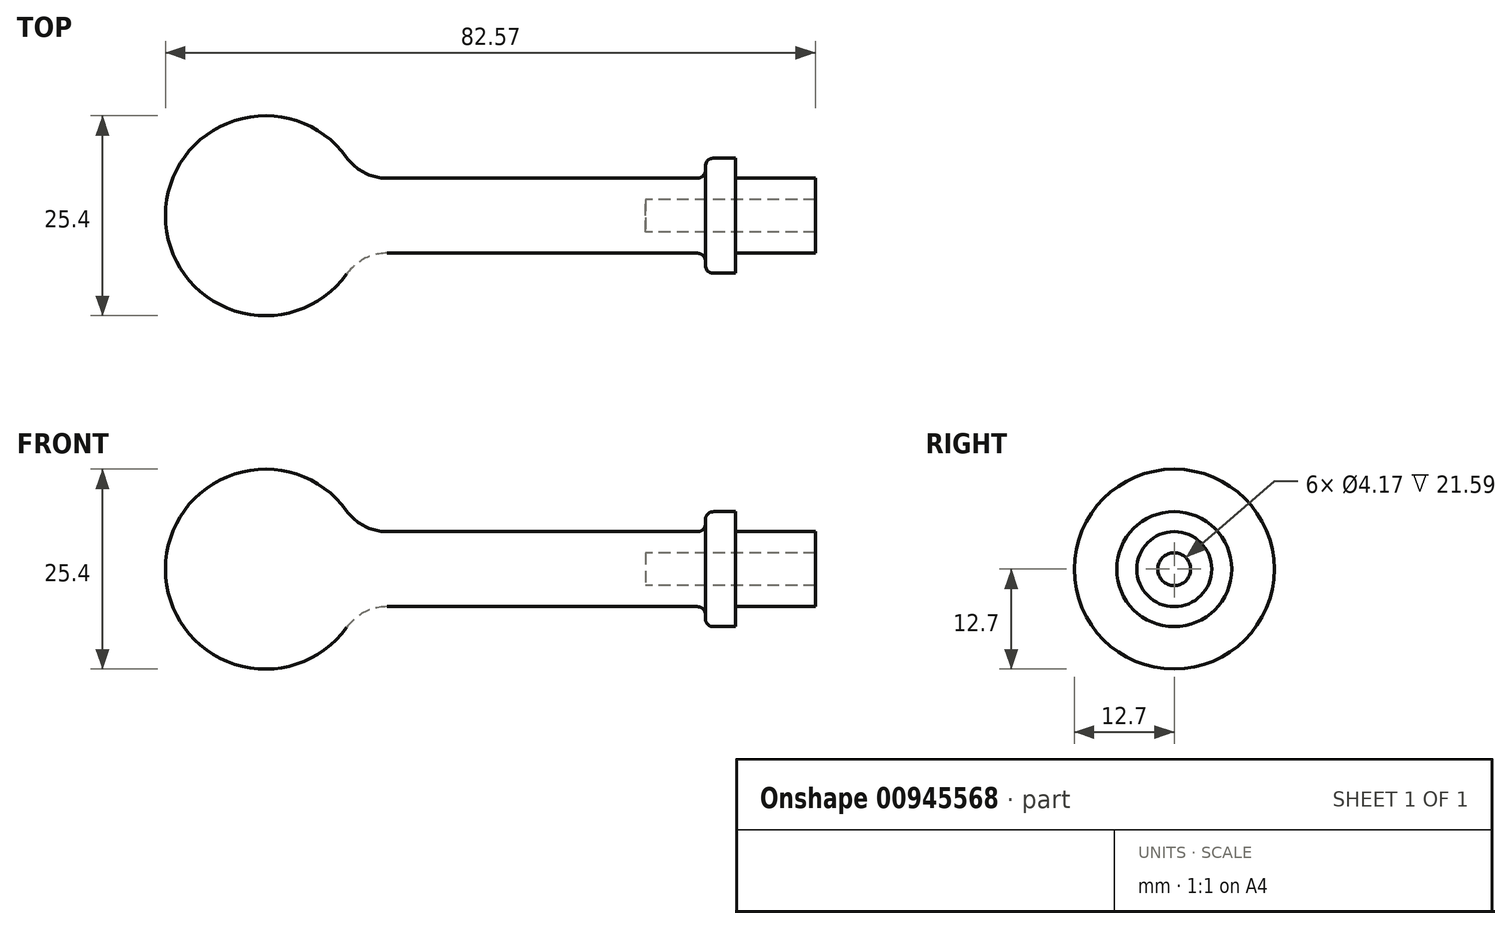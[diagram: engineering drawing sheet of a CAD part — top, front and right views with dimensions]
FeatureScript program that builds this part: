
annotation { "Feature Type Name" : "Feature", "Feature Type Description" : "" }
export const myFeature = defineFeature(function(context is Context, id is Id, definition is map)
    precondition{}
    {
        {
            var Q0;
            Q0=qCreatedBy(makeId("Top.planeOp"),FACE);
            var sketch = newSketch(context, id + "F0", { "sketchPlane" : qUnion([Q0])});
            skArc(sketch, "E0", {"start": v(10.32, 7.4) * mm, "mid": v(-3.9, 12.09) * mm, "end": v(-12.7, 0) * mm});
            skLineSegment(sketch, "E1.top", {"start": v(56.91, 7.3) * mm, "end": v(59.7, 7.3) * mm});
            skLineSegment(sketch, "E1.left", {"start": v(55.9, 5.78) * mm, "end": v(55.9, 6.29) * mm});
            skLineSegment(sketch, "E1.right", {"start": v(59.7, 4.76) * mm, "end": v(59.7, 7.3) * mm});
            skLineSegment(sketch, "E2.trimOffspring", {"start": v(15.47, 4.76) * mm, "end": v(54.88, 4.76) * mm});
            skLineSegment(sketch, "E3", {"start": v(-12.7, 0) * mm, "end": v(48.28, 0) * mm});
            skLineSegment(sketch, "E4.trimOffspring", {"start": v(59.7, 4.76) * mm, "end": v(69.87, 4.76) * mm});
            skArc(sketch, "E5.filletArc", {"start": v(10.32, 7.4) * mm, "mid": v(12.57, 5.46) * mm, "end": v(15.47, 4.76) * mm});
            skLineSegment(sketch, "E6", {"start": v(69.87, 4.76) * mm, "end": v(69.87, 2.08) * mm});
            skLineSegment(sketch, "E7", {"start": v(69.87, 2.08) * mm, "end": v(48.28, 2.08) * mm});
            skLineSegment(sketch, "E8", {"start": v(48.28, 2.08) * mm, "end": v(48.28, 0) * mm});
            skPoint(sketch, "E9.newPointA", {"position": v(57.15, 4.76) * mm});
            skArc(sketch, "E9.filletArc", {"start": v(54.88, 4.76) * mm, "mid": v(55.6, 5.06) * mm, "end": v(55.9, 5.78) * mm});
            skArc(sketch, "E10.filletArc", {"start": v(56.91, 7.3) * mm, "mid": v(56.2, 7) * mm, "end": v(55.9, 6.29) * mm});
            skSolve(sketch);
        }
        {
            var Q0;
            Q0=makeQuery(id+"F0.imprint","IMPRINT",FACE,{"disambiguationData":[TD([[makeQuery(id+"F0.imprint","IMPRINT",EDGE,{"derivedFrom":sQuery(id+"F0.wireOp",EDGE,"E0")}),1.0]])]});
            var Q1;
            Q1=sQuery(id+"F0.wireOp",EDGE,"E3");
            revolve(context, id + "F1", {"surfaceOperationType" : NewSurfaceOperationType.NEW, "entities" : qUnion([Q0]), "axis" : qUnion([Q1]), "revolveType" : RevolveType.FULL});
        }
    });
